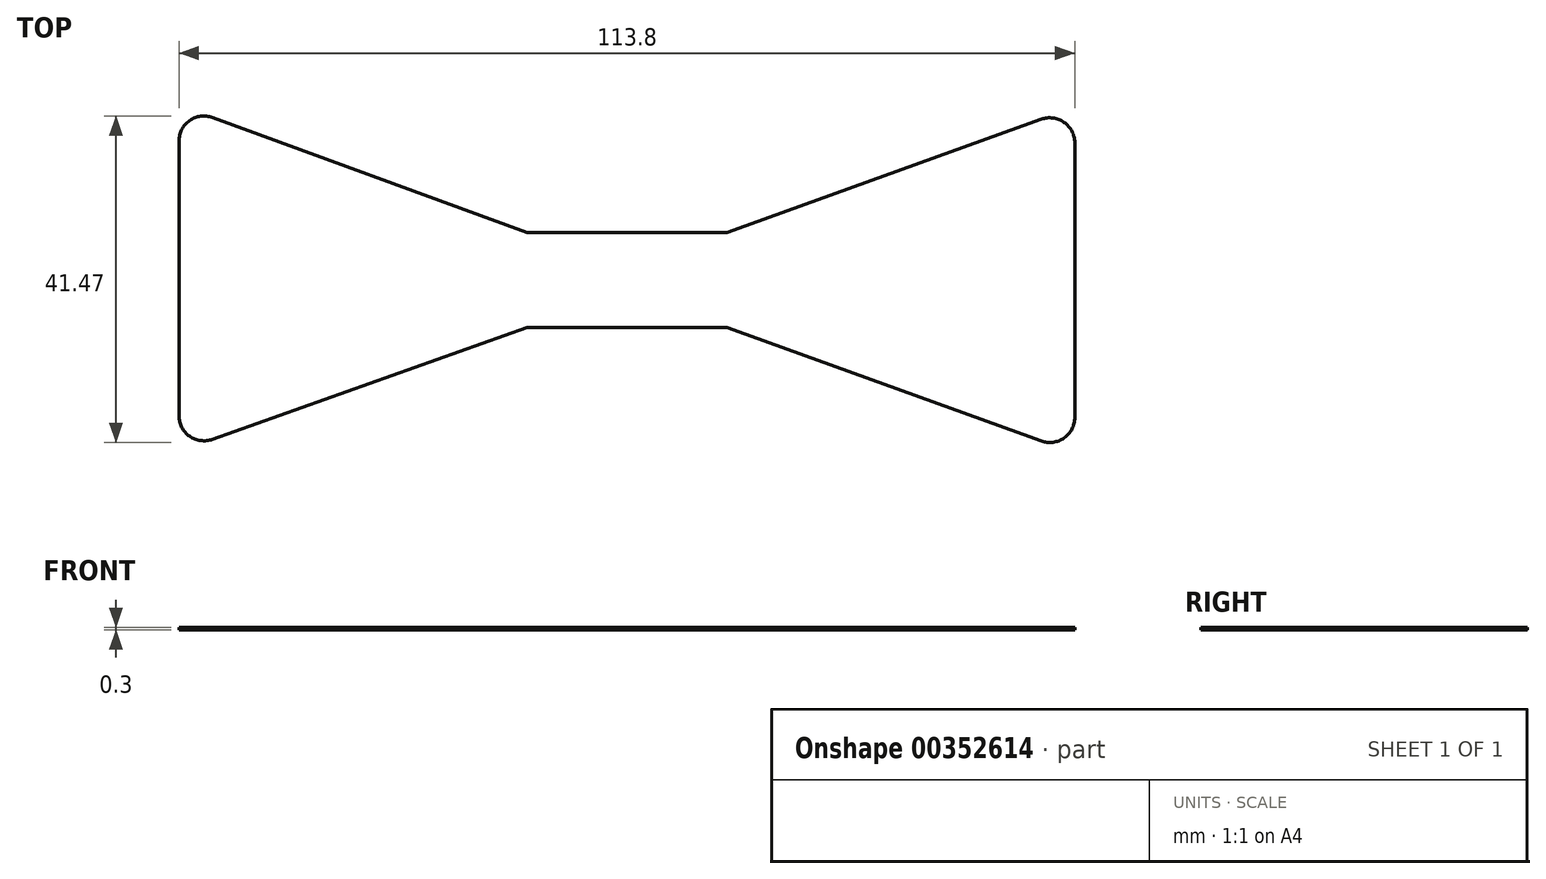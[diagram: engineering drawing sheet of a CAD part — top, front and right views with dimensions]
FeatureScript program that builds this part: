
annotation { "Feature Type Name" : "Feature", "Feature Type Description" : "" }
export const myFeature = defineFeature(function(context is Context, id is Id, definition is map)
    precondition{}
    {
        {
            var Q0;
            Q0=qCreatedBy(makeId("Top.planeOp"),FACE);
            var sketch = newSketch(context, id + "F0", { "sketchPlane" : qUnion([Q0])});
            skLineSegment(sketch, "E0.bottom", {"start": v(12.7, 5.4) * mm, "end": v(-12.7, 5.4) * mm});
            skLineSegment(sketch, "E0.top", {"start": v(12.7, -6.67) * mm, "end": v(-12.7, -6.67) * mm});
            skPoint(sketch, "E0.middle", {"position": v(0, -0.63) * mm});
            skLineSegment(sketch, "E1", {"start": v(-56.9, -0.4) * mm, "end": v(-56.9, 17.04) * mm});
            skLineSegment(sketch, "E2", {"start": v(-56.9, -0.4) * mm, "end": v(-56.9, -17.87) * mm});
            skLineSegment(sketch, "E3", {"start": v(56.9, -0.63) * mm, "end": v(56.9, 16.82) * mm});
            skLineSegment(sketch, "E4", {"start": v(56.9, -0.63) * mm, "end": v(56.9, -18.09) * mm});
            skLineSegment(sketch, "E5", {"start": v(12.7, 5.4) * mm, "end": v(52.64, 19.8) * mm});
            skLineSegment(sketch, "E6", {"start": v(12.7, -6.67) * mm, "end": v(52.64, -21.07) * mm});
            skLineSegment(sketch, "E7", {"start": v(-12.7, -6.67) * mm, "end": v(-52.66, -20.86) * mm});
            skLineSegment(sketch, "E8", {"start": v(-52.63, 20.02) * mm, "end": v(-12.7, 5.4) * mm});
            skPoint(sketch, "E9.visualSharp", {"position": v(-56.9, 21.58) * mm});
            skArc(sketch, "E9.filletArc", {"start": v(-52.63, 20.02) * mm, "mid": v(-55.54, 19.64) * mm, "end": v(-56.9, 17.04) * mm});
            skPoint(sketch, "E10.visualSharp", {"position": v(-56.9, -22.36) * mm});
            skArc(sketch, "E10.filletArc", {"start": v(-56.9, -17.87) * mm, "mid": v(-55.55, -20.46) * mm, "end": v(-52.66, -20.86) * mm});
            skPoint(sketch, "E11.visualSharp", {"position": v(56.9, -22.6) * mm});
            skArc(sketch, "E11.filletArc", {"start": v(52.64, -21.07) * mm, "mid": v(55.55, -20.68) * mm, "end": v(56.9, -18.09) * mm});
            skPoint(sketch, "E12.visualSharp", {"position": v(56.9, 21.34) * mm});
            skArc(sketch, "E12.filletArc", {"start": v(56.9, 16.82) * mm, "mid": v(55.55, 19.41) * mm, "end": v(52.64, 19.8) * mm});
            skLineSegment(sketch, "E13", {"start": v(-12.7, 5.4) * mm, "end": v(-12.7, -6.67) * mm});
            skLineSegment(sketch, "E14", {"start": v(12.7, 5.4) * mm, "end": v(12.7, -6.67) * mm});
            skSolve(sketch);
        }
        {
            var Q0;
            Q0 = qSketchRegion(id + "F0", true);
            extrude(context, id + "F1", {"entities" : qUnion([Q0]), "depth" : 0.3 * mm, "offsetDistance" : 25.4 * mm});
        }
    });
